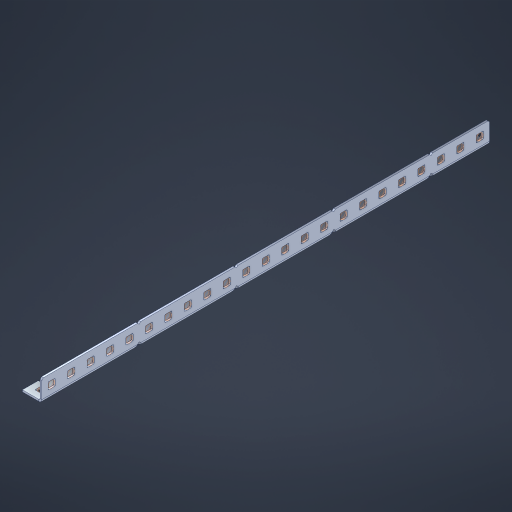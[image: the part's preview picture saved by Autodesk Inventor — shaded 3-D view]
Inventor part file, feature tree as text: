
AUTODESK INVENTOR PART (.ipt)
format: ipt  version: 2023 (Build 270158000, 158)  size: 1,032,192 bytes
history: native  units: in
note: dims shown in document units (in); Inventor stores cm internally (conversion verified against a paired STEP export)
features: other x76, extrude x67, sheet_metal_op x11, sketch x10, pattern_linear x2, mirror x1, chamfer x1
ambient origin geometry x8: Origin, YZ Plane, XZ Plane, XY Plane, X Axis, Y Axis, Z Axis, Center Point
bodies: Solid1 (feature_tree), Body (feature_tree)
feature tree (168):
  sheet_metal_op  "Flanges"
  other  "Flange Pattern Plane"
  other  "Flange Pattern Sketch"
  sheet_metal_op  "Flange Pattern"
  sheet_metal_op  "Body Pattern"
  pattern_linear  "Center Pattern"  Spacing1=0.0469in  [1 undecoded]
  other  "Arc Length"
  mirror  "Notch Mirror"
  pattern_linear  "Notch Pattern"  Spacing1=0.182in  [1 undecoded]
  chamfer  "End Chamfer"
  extrude  "Half Cut"  Depth=0.02in
  sketch  "Sketch1"  dims[d0=1.0in]
  other  "Plate1"
  sketch  "Sketch2"  dims[d1=11.5in]
  other  "Plate2"
  sheet_metal_op  "Bend1"
  sheet_metal_op  "Corner1"
  sketch  "Sketch3"  dims[d2=0.0469in]
  sketch  "Sketch7"  dims[d3=0.0469in]
  other  "Srf1"
  other  "Srf2"
  sketch  "Sketch8"  dims[d4=0.0234in]
  sketch  "Sketch9"  dims[d5=0.0938in]
  other  "Srf91"
  sheet_metal_op  "Body Pattern Sketch"
  other  "Srf92"
  sketch  "Sketch13"  dims[d6=0.0469in]
  sketch  "Sketch14"  dims[d7=0.5in d8=90.0deg d9=0.0312in]
  sketch  "Sketch15"  dims[d10=0.1875in]
  sketch  "Sketch16"  dims[d11=0.0469in d12=0.0469in d16=0.182in d17=0.02in d18=0.0469in d19=0.0in d20=0.25in d21=0.25in d38=9.0551in d40=0.5in d41=0.3937in d43=1.0in d46=0.172in d47=1.0in d48=0.0in d49=0.182in d50=0.02in d51=0.25in d52=0.25in d53=0.0469in d54=0.0in d55=0.172in d56=1.0in d57=0.0in d58=0.25in d60=9.0551in d62=0.5in d63=0.3937in d65=0.5in d85=0.1227in d86=0.1659in d88=0.04in d89=0.0469in d90=0.0in d91=0.04in d92=0.0491in d95=2.5in d96=0.04in d97=0.25in d98=45.0deg d99=0.25in d100=0.5in d101=0.0in d102=2.497in d106=0.182in d107=0.02in d108=0.5in d109=0.5in d110=0.0469in d111=0.0in d112=0.172in d113=0.5in d114=0.0in d117=0.5in d118=0.5in d119=0.5in]
  other  "Srf786"
  other  "Srf823"
  other  "Srf824"
  other  "Srf825"
  other  "Srf826"
  other  "Srf827"
  other  "Srf828"
  other  "Srf829"
  other  "Srf856"
  other  "Srf857"
  other  "Srf858"
  other  "Srf859"
  other  "Srf860"
  other  "Srf861"
  other  "Srf862"
  other  "Srf889"
  other  "Srf890"
  other  "Srf891"
  other  "Srf892"
  other  "Srf893"
  other  "Srf894"
  other  "Srf895"
  other  "Srf896"
  other  "Srf922"
  other  "Srf923"
  other  "Srf924"
  other  "Srf925"
  other  "Srf926"
  other  "Srf959"
  other  "Srf960"
  other  "Srf961"
  other  "Srf962"
  other  "Srf963"
  other  "Srf996"
  other  "Srf997"
  other  "Srf998"
  other  "Srf999"
  other  "Srf1000"
  other  "Srf1143"
  other  "Srf1144"
  other  "Srf1145"
  other  "Srf1146"
  other  "Srf1147"
  other  "Srf1148"
  other  "Srf1149"
  other  "Srf1150"
  other  "Srf1151"
  other  "Srf1199"
  other  "Srf1200"
  other  "Srf1201"
  other  "Srf1202"
  other  "Srf1203"
  other  "Srf1204"
  other  "Srf1205"
  other  "Srf1206"
  other  "Srf1207"
  other  "Srf1255"
  other  "Srf1256"
  other  "Srf1257"
  other  "Srf1258"
  other  "Srf1259"
  other  "Srf1260"
  other  "Srf1261"
  other  "Srf1262"
  other  "Srf1263"
  sheet_metal_op  "Flange Stamp"
  sheet_metal_op  "Flange Circle"
  sheet_metal_op  "Body Stamp"
  sheet_metal_op  "Body Circle"
  other  "Center Stamp"
  other  "Center Circle"
  sheet_metal_op  "Notch"
  extrude  "ExtrusionSrf2"  Depth=0.0469in
  extrude  "ExtrusionSrf92"  TaperAngle=0.0deg  [1 undecoded]
  extrude  "ExtrusionSrf823"  Depth=0.5in
  extrude  "ExtrusionSrf824"  Depth=0.5in
  extrude  "ExtrusionSrf825"  Depth=0.5in
  extrude  "ExtrusionSrf826"  Depth=0.5in
  extrude  "ExtrusionSrf827"  Depth=1.0in TaperAngle=0.0deg
  extrude  "ExtrusionSrf828"  Depth=0.182in
  extrude  "ExtrusionSrf829"  Depth=0.02in
  extrude  "ExtrusionSrf856"  Depth=0.5in
  extrude  "ExtrusionSrf857"  Depth=0.5in
  extrude  "ExtrusionSrf858"  Depth=0.0469in
  extrude  "ExtrusionSrf859"  TaperAngle=0.0deg  [1 undecoded]
  extrude  "ExtrusionSrf860"  Depth=0.5in
  extrude  "ExtrusionSrf861"  Depth=1.0in TaperAngle=0.0deg
  extrude  "ExtrusionSrf862"  Depth=0.5in
  extrude  "ExtrusionSrf889"  Depth=0.5in
  extrude  "ExtrusionSrf890"  Depth=0.5in
  extrude  "ExtrusionSrf891"  Depth=0.5in
  extrude  "ExtrusionSrf892"  Depth=0.5in
  extrude  "ExtrusionSrf893"  Depth=0.5in
  extrude  "ExtrusionSrf894"  Depth=0.0469in
  extrude  "ExtrusionSrf895"  TaperAngle=0.0deg  [1 undecoded]
  extrude  "ExtrusionSrf896"  Depth=0.5in
  extrude  "ExtrusionSrf922"  Depth=0.5in
  extrude  "ExtrusionSrf923"  Depth=0.5in
  extrude  "ExtrusionSrf924"  Depth=0.5in TaperAngle=45.0deg
  extrude  "ExtrusionSrf925"  Depth=0.5in
  extrude  "ExtrusionSrf926"  Depth=0.5in TaperAngle=0.0deg
  extrude  "ExtrusionSrf959"  Depth=0.5in
  extrude  "ExtrusionSrf960"  Depth=0.182in
  extrude  "ExtrusionSrf961"  Depth=0.02in
  extrude  "ExtrusionSrf962"  Depth=0.5in
  extrude  "ExtrusionSrf963"  Depth=0.5in
  extrude  "ExtrusionSrf996"  Depth=0.0469in
  extrude  "ExtrusionSrf997"  TaperAngle=0.0deg  [1 undecoded]
  extrude  "ExtrusionSrf998"  Depth=0.5in
  extrude  "ExtrusionSrf999"  Depth=0.5in TaperAngle=0.0deg
  extrude  "ExtrusionSrf1000"  Depth=0.5in
  extrude  "ExtrusionSrf1143"  Depth=0.5in
  extrude  "ExtrusionSrf1144"  Depth=0.5in
  extrude  "ExtrusionSrf1145"  [1 undecoded]
  extrude  "ExtrusionSrf1146"  [1 undecoded]
  extrude  "ExtrusionSrf1147"  [1 undecoded]
  extrude  "ExtrusionSrf1148"  [1 undecoded]
  extrude  "ExtrusionSrf1149"  [1 undecoded]
  extrude  "ExtrusionSrf1150"  [1 undecoded]
  extrude  "ExtrusionSrf1151"  [1 undecoded]
  extrude  "ExtrusionSrf1199"  [1 undecoded]
  extrude  "ExtrusionSrf1200"  [1 undecoded]
  extrude  "ExtrusionSrf1201"  [1 undecoded]
  extrude  "ExtrusionSrf1202"  [1 undecoded]
  extrude  "ExtrusionSrf1203"  [1 undecoded]
  extrude  "ExtrusionSrf1204"  [1 undecoded]
  extrude  "ExtrusionSrf1205"  [1 undecoded]
  extrude  "ExtrusionSrf1206"  [1 undecoded]
  extrude  "ExtrusionSrf1207"  [1 undecoded]
  extrude  "ExtrusionSrf1255"  [1 undecoded]
  extrude  "ExtrusionSrf1256"  [1 undecoded]
  extrude  "ExtrusionSrf1257"  [1 undecoded]
  extrude  "ExtrusionSrf1258"  [1 undecoded]
  extrude  "ExtrusionSrf1259"  [1 undecoded]
  extrude  "ExtrusionSrf1260"  [1 undecoded]
  extrude  "ExtrusionSrf1261"  [1 undecoded]
  extrude  "ExtrusionSrf1262"  [1 undecoded]
  extrude  "ExtrusionSrf1263"  [1 undecoded]
note: 31 required parameter values undecoded (feature->parameter linkage not recoverable at this tier; creation-order binding heuristic only, values carry confidence <= 0.55)
